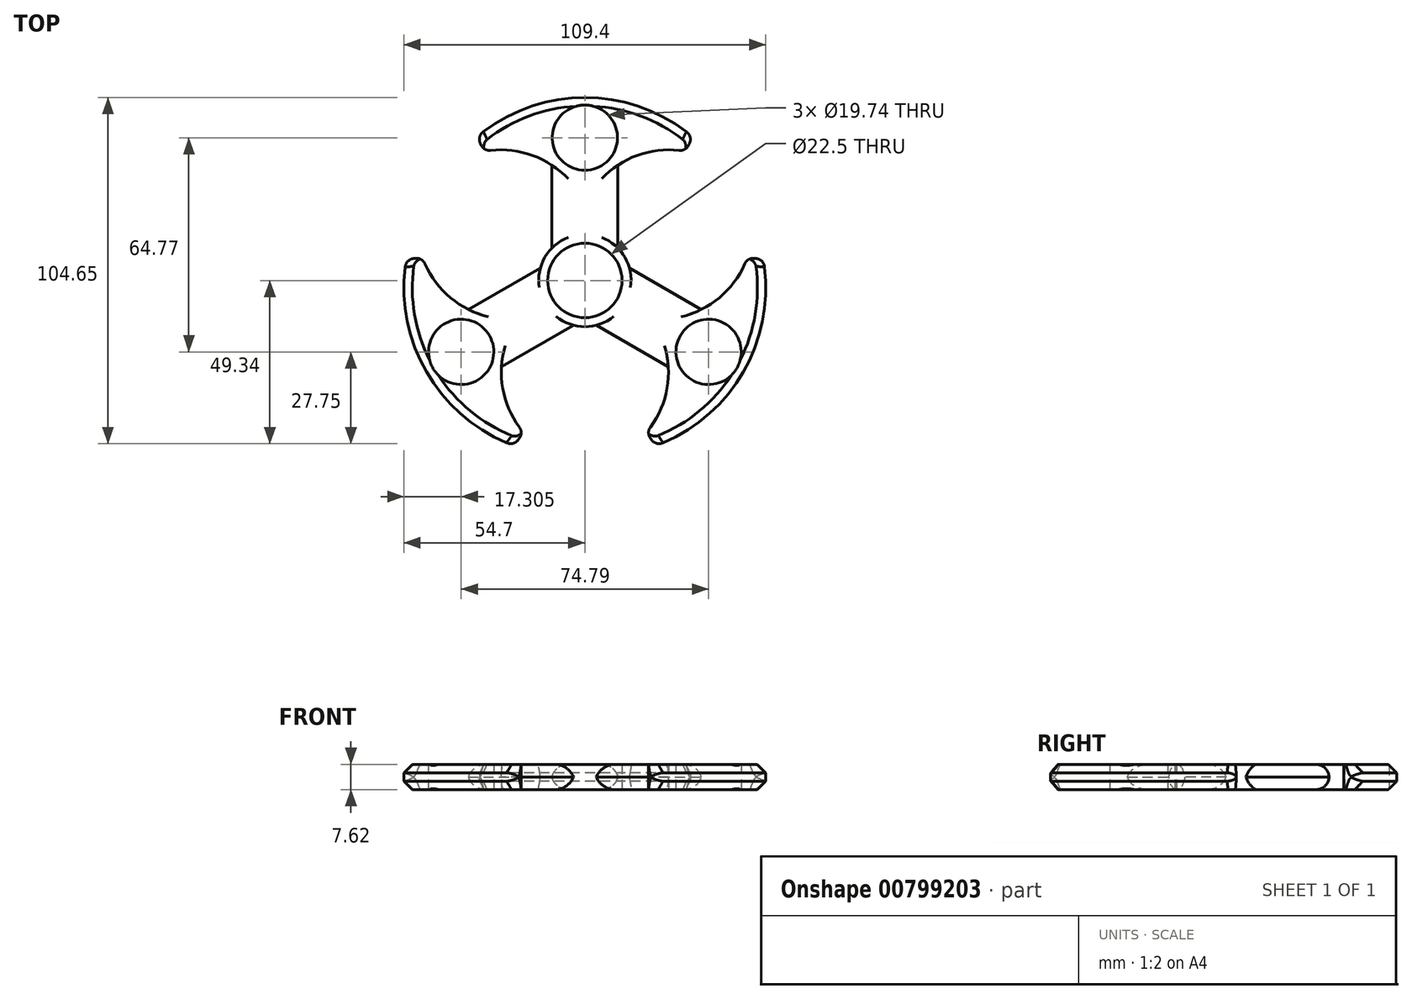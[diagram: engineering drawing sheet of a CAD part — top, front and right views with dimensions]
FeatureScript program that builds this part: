
annotation { "Feature Type Name" : "Feature", "Feature Type Description" : "" }
export const myFeature = defineFeature(function(context is Context, id is Id, definition is map)
    precondition{}
    {
        {
            var Q0;
            Q0=qCreatedBy(makeId("Top.planeOp"),FACE);
            var sketch = newSketch(context, id + "F0", { "sketchPlane" : qUnion([Q0])});
            skCircle(sketch, "E0", {"center": v(0, 0) * mm, "radius": 11.25 * mm});
            skCircle(sketch, "E1", {"center": v(0, 0) * mm, "radius": 13.97 * mm});
            skLineSegment(sketch, "E2", {"start": v(-10.16, 9.59) * mm, "end": v(-10.16, 34.99) * mm});
            skLineSegment(sketch, "E3", {"start": v(10.16, 9.59) * mm, "end": v(10.16, 34.99) * mm});
            skArc(sketch, "E4", {"start": v(-10.16, 34.99) * mm, "mid": v(-25.4, 39.51) * mm, "end": v(-40.64, 34.99) * mm});
            skArc(sketch, "E5", {"start": v(40.64, 34.99) * mm, "mid": v(25.4, 39.51) * mm, "end": v(10.16, 34.99) * mm});
            skArc(sketch, "E6", {"start": v(40.64, 34.99) * mm, "mid": v(0, 55.3) * mm, "end": v(-40.64, 34.99) * mm});
            skArc(sketch, "E7.1.0", {"start": v(-50.62, 17.7) * mm, "mid": v(-47.9, -27.65) * mm, "end": v(-9.98, -52.69) * mm});
            skArc(sketch, "E7.1.1", {"start": v(-25.22, -26.3) * mm, "mid": v(-21.52, -41.75) * mm, "end": v(-9.98, -52.69) * mm});
            skLineSegment(sketch, "E7.1.2", {"start": v(-3.22, -13.6) * mm, "end": v(-25.22, -26.3) * mm});
            skLineSegment(sketch, "E7.1.3", {"start": v(-13.38, 4) * mm, "end": v(-35.38, -8.7) * mm});
            skArc(sketch, "E7.1.4", {"start": v(-50.62, 17.7) * mm, "mid": v(-46.92, 2.24) * mm, "end": v(-35.38, -8.7) * mm});
            skArc(sketch, "E7.2.0", {"start": v(9.98, -52.69) * mm, "mid": v(47.9, -27.65) * mm, "end": v(50.62, 17.7) * mm});
            skArc(sketch, "E7.2.1", {"start": v(35.38, -8.7) * mm, "mid": v(46.92, 2.24) * mm, "end": v(50.62, 17.7) * mm});
            skLineSegment(sketch, "E7.2.2", {"start": v(13.38, 4) * mm, "end": v(35.38, -8.7) * mm});
            skLineSegment(sketch, "E7.2.3", {"start": v(3.22, -13.6) * mm, "end": v(25.22, -26.3) * mm});
            skArc(sketch, "E7.2.4", {"start": v(9.98, -52.69) * mm, "mid": v(21.52, -41.75) * mm, "end": v(25.22, -26.3) * mm});
            skCircle(sketch, "E8", {"center": v(0, 43.18) * mm, "radius": 9.87 * mm});
            skCircle(sketch, "E9.1.0", {"center": v(-37.4, -21.59) * mm, "radius": 9.87 * mm});
            skCircle(sketch, "E9.2.0", {"center": v(37.4, -21.6) * mm, "radius": 9.87 * mm});
            skSolve(sketch);
        }
        {
            var Q0;
            {var subQ1=sQuery(id+"F0.wireOp",EDGE,"E2");Q0=makeQuery(id+"F0.imprint","IMPRINT",FACE,{"disambiguationData":[TD([[makeQuery(id+"F0.imprint","IMPRINT",EDGE,{"derivedFrom":subQ1}),-1.0]])]});}
            var Q1;
            Q1=makeQuery(id+"F0.imprint","IMPRINT",FACE,{"disambiguationData":[TD([[makeQuery(id+"F0.imprint","IMPRINT",EDGE,{"derivedFrom":sQuery(id+"F0.wireOp",EDGE,"E7.1.0")}),1.0]])]});
            var Q2;
            Q2=makeQuery(id+"F0.imprint","IMPRINT",FACE,{"disambiguationData":[TD([[makeQuery(id+"F0.imprint","IMPRINT",EDGE,{"derivedFrom":sQuery(id+"F0.wireOp",EDGE,"E7.2.0")}),1.0]])]});
            var Q3;
            Q3=makeQuery(id+"F0.imprint","IMPRINT",FACE,{"disambiguationData":[TD([[makeQuery(id+"F0.imprint","IMPRINT",EDGE,{"derivedFrom":sQuery(id+"F0.wireOp",EDGE,"E0")}),-1.0]])]});
            extrude(context, id + "F1", {"entities" : qUnion([Q0, Q1, Q2, Q3]), "depth" : 7.62 * mm, "offsetDistance" : 25.4 * mm});
        }
        {
            var Q0;
            Q0=makeQuery(id+"F1.opExtrude","CAP_EDGE",EDGE,{"disambiguationData":[OSD([sQuery(id+"F0.wireOp",EDGE,"E7.1.2")])],"isStart":false});
            var Q1;
            Q1=makeQuery(id+"F1.opExtrude","CAP_EDGE",EDGE,{"disambiguationData":[OSD([sQuery(id+"F0.wireOp",EDGE,"E7.1.3")])],"isStart":false});
            var Q2;
            Q2=makeQuery(id+"F1.opExtrude","CAP_EDGE",EDGE,{"disambiguationData":[OSD([sQuery(id+"F0.wireOp",EDGE,"E2")])],"isStart":false});
            var Q3;
            Q3=makeQuery(id+"F1.opExtrude","CAP_EDGE",EDGE,{"disambiguationData":[OSD([sQuery(id+"F0.wireOp",EDGE,"E3")])],"isStart":false});
            var Q4;
            Q4=makeQuery(id+"F1.opExtrude","CAP_EDGE",EDGE,{"disambiguationData":[OSD([sQuery(id+"F0.wireOp",EDGE,"E7.2.2")])],"isStart":false});
            var Q5;
            Q5=makeQuery(id+"F1.opExtrude","CAP_EDGE",EDGE,{"disambiguationData":[OSD([sQuery(id+"F0.wireOp",EDGE,"E7.2.3")])],"isStart":false});
            var Q6;
            Q6=makeQuery(id+"F1.opExtrude","CAP_EDGE",EDGE,{"disambiguationData":[OSD([sQuery(id+"F0.wireOp",EDGE,"E7.1.3")])],"isStart":true});
            var Q7;
            Q7=makeQuery(id+"F1.opExtrude","CAP_EDGE",EDGE,{"disambiguationData":[OSD([sQuery(id+"F0.wireOp",EDGE,"E7.1.2")])],"isStart":true});
            var Q8;
            Q8=makeQuery(id+"F1.opExtrude","CAP_EDGE",EDGE,{"disambiguationData":[OSD([sQuery(id+"F0.wireOp",EDGE,"E7.2.3")])],"isStart":true});
            var Q9;
            Q9=makeQuery(id+"F1.opExtrude","CAP_EDGE",EDGE,{"disambiguationData":[OSD([sQuery(id+"F0.wireOp",EDGE,"E7.2.2")])],"isStart":true});
            var Q10;
            Q10=makeQuery(id+"F1.opExtrude","CAP_EDGE",EDGE,{"disambiguationData":[OSD([sQuery(id+"F0.wireOp",EDGE,"E3")])],"isStart":true});
            var Q11;
            Q11=makeQuery(id+"F1.opExtrude","CAP_EDGE",EDGE,{"disambiguationData":[OSD([sQuery(id+"F0.wireOp",EDGE,"E2")])],"isStart":true});
            fillet(context, id + "F2", {"entities" : qUnion([Q0, Q1, Q2, Q3, Q4, Q5, Q6, Q7, Q8, Q9, Q10, Q11]), "radius" : 5.08 * mm, "tangentPropagation" : true, "allowEdgeOverflow" : false});
        }
        {
            var Q0;
            Q0=makeQuery(id+"F1.opExtrude","CAP_EDGE",EDGE,{"disambiguationData":[OSD([sQuery(id+"F0.wireOp",EDGE,"E7.1.0")])],"isStart":false});
            var Q1;
            Q1=makeQuery(id+"F1.opExtrude","CAP_EDGE",EDGE,{"disambiguationData":[OSD([sQuery(id+"F0.wireOp",EDGE,"E6")])],"isStart":false});
            var Q2;
            Q2=makeQuery(id+"F1.opExtrude","CAP_EDGE",EDGE,{"disambiguationData":[OSD([sQuery(id+"F0.wireOp",EDGE,"E7.2.0")])],"isStart":false});
            var Q3;
            Q3=makeQuery(id+"F1.opExtrude","CAP_EDGE",EDGE,{"disambiguationData":[OSD([sQuery(id+"F0.wireOp",EDGE,"E7.2.0")])],"isStart":true});
            var Q4;
            Q4=makeQuery(id+"F1.opExtrude","CAP_EDGE",EDGE,{"disambiguationData":[OSD([sQuery(id+"F0.wireOp",EDGE,"E6")])],"isStart":true});
            var Q5;
            Q5=makeQuery(id+"F1.opExtrude","SWEPT_FACE",FACE,{"disambiguationData":[OSD([sQuery(id+"F0.wireOp",EDGE,"E7.1.0")])]});
            var Q6;
            Q6=makeQuery(id+"F1.opExtrude","SWEPT_EDGE",EDGE,{"disambiguationData":[OSD([sQuery(id+"F0.wireOp",EDGE,"E4"),sQuery(id+"F0.wireOp",EDGE,"E6")])]});
            var Q7;
            Q7=makeQuery(id+"F1.opExtrude","SWEPT_EDGE",EDGE,{"disambiguationData":[OSD([sQuery(id+"F0.wireOp",EDGE,"E5"),sQuery(id+"F0.wireOp",EDGE,"E6")])]});
            var Q8;
            Q8=makeQuery(id+"F1.opExtrude","SWEPT_FACE",FACE,{"disambiguationData":[OSD([sQuery(id+"F0.wireOp",EDGE,"E7.2.0")])]});
            chamfer(context, id + "F3", {"entities" : qUnion([Q0, Q1, Q2, Q3, Q4, Q5, Q6, Q7, Q8]), "width" : 2.54 * mm, "tangentPropagation" : true});
        }
        {
            var Q0;
            Q0=makeQuery(id+"F3.opChamfer","BLEND_FACE",FACE,{"disambiguationData":[OSD([sQuery(id+"F0.wireOp",EDGE,"E7.2.0"),sQuery(id+"F0.wireOp",EDGE,"E7.2.1")])]});
            var Q1;
            Q1=makeQuery(id+"F3.opChamfer","BLEND_FACE",FACE,{"disambiguationData":[OSD([sQuery(id+"F0.wireOp",EDGE,"E7.2.0"),sQuery(id+"F0.wireOp",EDGE,"E7.2.4")])]});
            var Q2;
            Q2=makeQuery(id+"F3.opChamfer","BLEND_FACE",FACE,{"disambiguationData":[OSD([sQuery(id+"F0.wireOp",EDGE,"E7.1.0"),sQuery(id+"F0.wireOp",EDGE,"E7.1.1")])]});
            var Q3;
            Q3=makeQuery(id+"F3.opChamfer","BLEND_FACE",FACE,{"disambiguationData":[OSD([sQuery(id+"F0.wireOp",EDGE,"E7.1.0"),sQuery(id+"F0.wireOp",EDGE,"E7.1.4")])]});
            var Q4;
            Q4=makeQuery(id+"F3.opChamfer","BLEND_FACE",FACE,{"disambiguationData":[OSD([sQuery(id+"F0.wireOp",EDGE,"E4"),sQuery(id+"F0.wireOp",EDGE,"E6")])]});
            var Q5;
            Q5=makeQuery(id+"F3.opChamfer","BLEND_FACE",FACE,{"disambiguationData":[OSD([sQuery(id+"F0.wireOp",EDGE,"E5"),sQuery(id+"F0.wireOp",EDGE,"E6")])]});
            fillet(context, id + "F4", {"entities" : qUnion([Q0, Q1, Q2, Q3, Q4, Q5]), "radius" : 2.8 * mm, "tangentPropagation" : true, "allowEdgeOverflow" : false});
        }
    });
